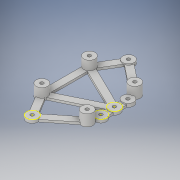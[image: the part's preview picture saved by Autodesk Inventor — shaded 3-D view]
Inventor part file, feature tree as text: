
AUTODESK INVENTOR PART (.ipt)
format: ipt  version: 2019 (Build 230136000, 136)  size: 285,696 bytes
history: native  units: mm
features: sketch x9, extrude x4, projected_geometry x3, hole x2
ambient origin geometry x8: Origin, YZ Plane, XZ Plane, XY Plane, X Axis, Y Axis, Z Axis, Center Point
bodies: Solid1 (feature_tree)
feature tree (18):
  sketch  "Sketch1"  dims[d0=85.0mm d1=12.0mm]
  extrude  "Extrusion1"  Depth=12.0mm
  hole  "Hole1"  [1 undecoded]
  sketch  "Sketch Driven Pattern1"  dims[d2=12.0mm d3=30.0mm]
  sketch  "Sketch4"  dims[d9=3.0mm d10=6.0mm d11=10.0mm d12=2.0mm d13=90.0deg d14=8.0mm d15=0.0mm d16=40.0mm]
  extrude  "Extrusion2"  Depth=30.5mm
  hole  "Hole2"  [1 undecoded]
  extrude  "Extrusion3"  Depth=8.0mm
  extrude  "Extrusion4"  Depth=3.0mm
  sketch  "Sketch2"  dims[d4=30.5mm d5=30.5mm]
  sketch  "Sketch3"  dims[d6=10.0mm d7=3.0mm d8=0.0mm]
  projected_geometry  "Projected Loop1"
  sketch  "Sketch5"  dims[d17=42.0mm d18=3.0mm]
  sketch  "Sketch7"  dims[d19=21.5mm]
  sketch  "Sketch8"  dims[d20=21.5mm]
  sketch  "Sketch9"  dims[d21=10.0mm d22=10.0mm d23=10.0mm d24=10.0mm d25=10.0mm d26=0.0mm d27=3.0mm d28=6.0mm d29=10.0mm d30=2.0mm d31=90.0deg d32=8.0mm d33=0.0mm d34=6.0mm d35=6.0mm d36=6.0mm d37=6.0mm d38=6.0mm d39=6.0mm d40=2.0mm d41=0.0mm d42=6.0mm d43=6.0mm d44=2.0mm d45=0.0mm]
  projected_geometry  "Project Cut Edges1"
  projected_geometry  "Project Cut Edges2"
note: 2 required parameter values undecoded (feature->parameter linkage not recoverable at this tier; creation-order binding heuristic only, values carry confidence <= 0.55)
